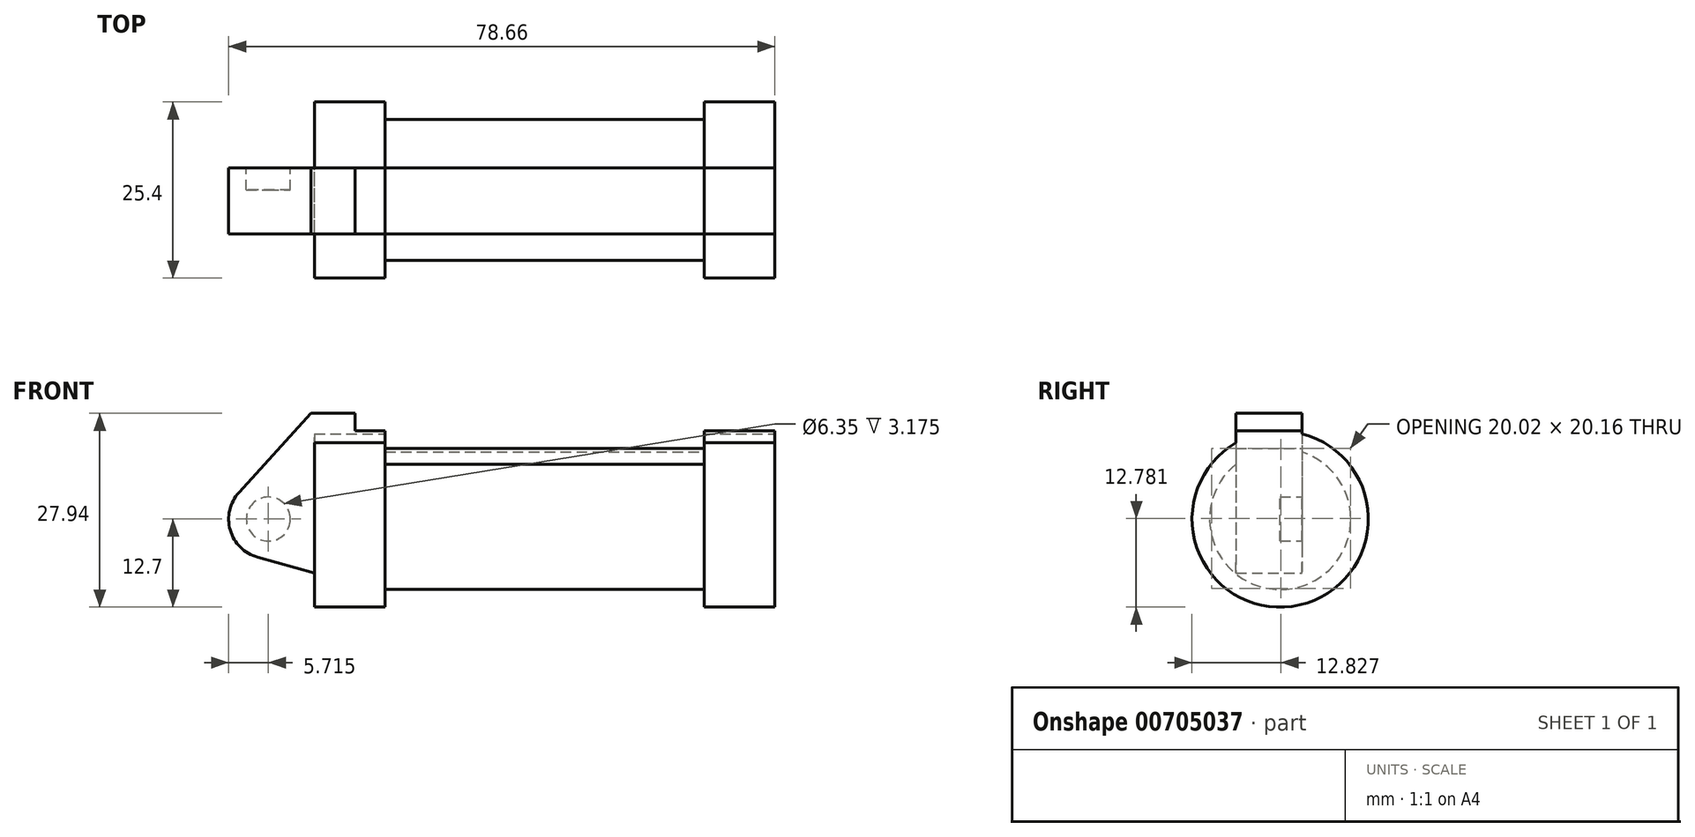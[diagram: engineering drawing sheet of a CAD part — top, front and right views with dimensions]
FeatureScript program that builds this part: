
annotation { "Feature Type Name" : "Feature", "Feature Type Description" : "" }
export const myFeature = defineFeature(function(context is Context, id is Id, definition is map)
    precondition{}
    {
        {
            var Q0;
            Q0=qCreatedBy(makeId("Front.planeOp"),FACE);
            var sketch = newSketch(context, id + "F0", { "sketchPlane" : qUnion([Q0])});
            skLineSegment(sketch, "E0", {"start": v(0, 0) * mm, "end": v(0, 12.7) * mm});
            skLineSegment(sketch, "E1", {"start": v(0, 12.7) * mm, "end": v(10.16, 12.7) * mm});
            skLineSegment(sketch, "E2", {"start": v(10.16, 12.7) * mm, "end": v(10.16, 10.16) * mm});
            skLineSegment(sketch, "E3", {"start": v(10.16, 10.16) * mm, "end": v(56.13, 10.16) * mm});
            skLineSegment(sketch, "E4", {"start": v(56.13, 10.16) * mm, "end": v(56.13, 12.7) * mm});
            skLineSegment(sketch, "E5", {"start": v(56.13, 12.7) * mm, "end": v(66.3, 12.7) * mm});
            skLineSegment(sketch, "E6", {"start": v(66.3, 12.7) * mm, "end": v(66.3, 0) * mm});
            skLineSegment(sketch, "E7", {"start": v(66.3, 0) * mm, "end": v(0, 0) * mm});
            skLineSegment(sketch, "E8", {"start": v(5.84, 15.24) * mm, "end": v(-0.5, 15.24) * mm});
            skLineSegment(sketch, "E9", {"start": v(-0.5, 15.24) * mm, "end": v(-10.88, 3.85) * mm});
            skLineSegment(sketch, "E10", {"start": v(0, 0) * mm, "end": v(-6.65, 0) * mm});
            skCircle(sketch, "E11", {"center": v(-6.65, 0) * mm, "radius": 5.72 * mm});
            skCircle(sketch, "E12", {"center": v(-6.65, 0) * mm, "radius": 3.18 * mm});
            skLineSegment(sketch, "E13", {"start": v(5.84, 15.24) * mm, "end": v(5.84, -9.4) * mm});
            skLineSegment(sketch, "E14", {"start": v(5.84, -9.4) * mm, "end": v(-8.18, -5.5) * mm});
            skSolve(sketch);
        }
        {
            var Q0;
            {var subQ0=sQuery(id+"F0.wireOp",EDGE,"E2");Q0=makeQuery(id+"F0.imprint","IMPRINT",FACE,{"disambiguationData":[TD([[makeQuery(id+"F0.imprint","IMPRINT",EDGE,{"derivedFrom":subQ0}),-1.0]])]});}
            var Q1;
            {var subQ0=sQuery(id+"F0.wireOp",EDGE,"E0");Q1=makeQuery(id+"F0.imprint","IMPRINT",FACE,{"disambiguationData":[TD([[makeQuery(id+"F0.imprint","IMPRINT",EDGE,{"derivedFrom":subQ0}),-1.0]])]});}
            var Q2;
            Q2=sQuery(id+"F0.wireOp",EDGE,"E7");
            revolve(context, id + "F1", {"entities" : qUnion([Q0, Q1]), "axis" : qUnion([Q2]), "revolveType" : RevolveType.FULL});
        }
        {
            var Q0;
            {var subQ0=sQuery(id+"F0.wireOp",EDGE,"E2");Q0=makeQuery(id+"F0.imprint","IMPRINT",FACE,{"disambiguationData":[TD([[makeQuery(id+"F0.imprint","IMPRINT",EDGE,{"derivedFrom":subQ0}),-1.0]])]});}
            var Q1;
            {var subQ0=sQuery(id+"F0.wireOp",EDGE,"E12");Q1=makeQuery(id+"F0.imprint","IMPRINT",FACE,{"disambiguationData":[TD([[makeQuery(id+"F0.imprint","IMPRINT",EDGE,{"derivedFrom":subQ0}),1.0]])]});}
            var Q2;
            {var subQ0=sQuery(id+"F0.wireOp",EDGE,"E0");Q2=makeQuery(id+"F0.imprint","IMPRINT",FACE,{"disambiguationData":[TD([[makeQuery(id+"F0.imprint","IMPRINT",EDGE,{"derivedFrom":subQ0}),-1.0]])]});}
            var Q3;
            {var subQ0=sQuery(id+"F0.wireOp",EDGE,"E14");Q3=makeQuery(id+"F0.imprint","IMPRINT",FACE,{"disambiguationData":[TD([[makeQuery(id+"F0.imprint","IMPRINT",EDGE,{"derivedFrom":subQ0}),-1.0]])]});}
            var Q4;
            {var subQ5=sQuery(id+"F0.wireOp",EDGE,"E12");Q4=makeQuery(id+"F0.imprint","IMPRINT",FACE,{"disambiguationData":[TD([[makeQuery(id+"F0.imprint","IMPRINT",EDGE,{"derivedFrom":subQ5}),-1.0]])]});}
            extrude(context, id + "F2", {"entities" : qUnion([Q0, Q1, Q2, Q3, Q4]), "operationType" : NewBodyOperationType.ADD, "depth" : 6.35 * mm, "offsetDistance" : 25.4 * mm});
        }
        {
            var Q0;
            {var subQ1=sQuery(id+"F0.wireOp",EDGE,"E0");Q0=makeQuery(id+"F0.imprint","IMPRINT",FACE,{"disambiguationData":[TD([[makeQuery(id+"F0.imprint","IMPRINT",EDGE,{"derivedFrom":subQ1}),1.0]])]});}
            extrude(context, id + "F3", {"entities" : qUnion([Q0]), "operationType" : NewBodyOperationType.ADD, "depth" : 6.35 * mm, "offsetDistance" : 25.4 * mm});
        }
        {
            var Q0;
            Q0 = qSketchRegion(id + "F0", true);
            extrude(context, id + "F4", {"entities" : qUnion([Q0]), "operationType" : NewBodyOperationType.ADD, "endBound" : BoundingType.SYMMETRIC, "depth" : 6.35 * mm, "offsetDistance" : 25.4 * mm});
        }
        {
            var Q0;
            Q0 = qSketchRegion(id + "F0", true);
            extrude(context, id + "F5", {"entities" : qUnion([Q0]), "operationType" : NewBodyOperationType.ADD, "endBound" : BoundingType.SYMMETRIC, "oppositeDirection" : true, "depth" : 6.35 * mm, "offsetDistance" : 25.4 * mm});
        }
        {
            var Q0;
            Q0=sQuery(id+"F0.wireOp",EDGE,"E12");
            extrude(context, id + "F6", {"bodyType" : ToolBodyType.SURFACE, "surfaceEntities" : qUnion([Q0]), "depth" : 25.4 * mm, "offsetDistance" : 25.4 * mm});
        }
        {
            var Q0;
            Q0=makeQuery(id+"F6.opExtrude","SWEPT_BODY",BODY,{"disambiguationData":[OSD([sQuery(id+"F0.wireOp",EDGE,"E12")])]});
            deleteBodies(context, id + "F7", {"entities" : qUnion([Q0])});
        }
    });
